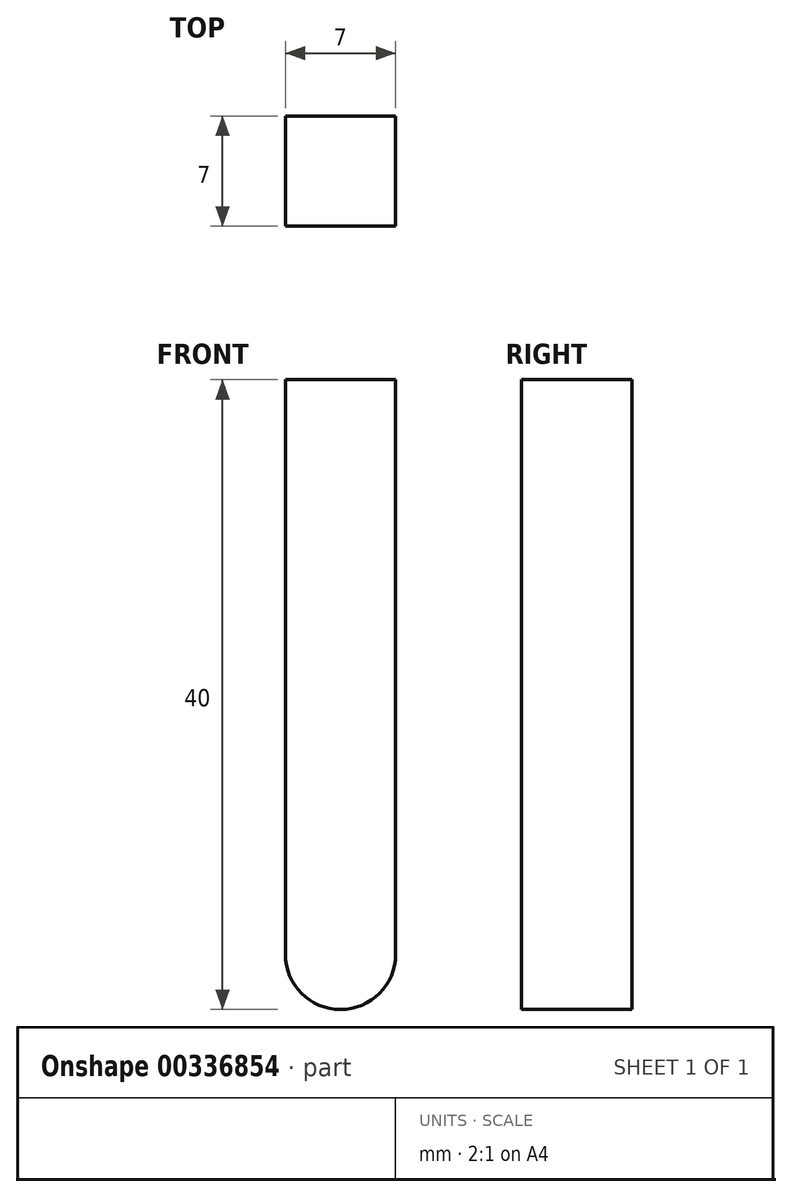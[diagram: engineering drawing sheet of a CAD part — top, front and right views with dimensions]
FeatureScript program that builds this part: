
annotation { "Feature Type Name" : "Feature", "Feature Type Description" : "" }
export const myFeature = defineFeature(function(context is Context, id is Id, definition is map)
    precondition{}
    {
        {
            var Q0;
            Q0=qCreatedBy(makeId("Front.planeOp"),FACE);
            var sketch = newSketch(context, id + "F0", { "sketchPlane" : qUnion([Q0])});
            skLineSegment(sketch, "E0.bottom", {"start": v(3.5, 20) * mm, "end": v(-3.5, 20) * mm});
            skLineSegment(sketch, "E0.top", {"start": v(3.5, -20) * mm, "end": v(-3.5, -20) * mm});
            skLineSegment(sketch, "E0.left", {"start": v(3.5, 20) * mm, "end": v(3.5, -20) * mm});
            skLineSegment(sketch, "E0.right", {"start": v(-3.5, 20) * mm, "end": v(-3.5, -20) * mm});
            skPoint(sketch, "E0.middle", {"position": v(0, 0) * mm});
            skSolve(sketch);
        }
        {
            var Q0;
            Q0=makeQuery(id+"F0.imprint","IMPRINT",FACE,{"disambiguationData":[TD([[makeQuery(id+"F0.imprint","IMPRINT",EDGE,{"derivedFrom":sQuery(id+"F0.wireOp",EDGE,"E0.bottom")}),1.0]])]});
            extrude(context, id + "F1", {"entities" : qUnion([Q0]), "depth" : 7 * mm});
        }
        {
            var Q0;
            Q0=makeQuery(id+"F1.opExtrude","SWEPT_EDGE",EDGE,{"disambiguationData":[OSD([sQuery(id+"F0.wireOp",EDGE,"E0.top"),sQuery(id+"F0.wireOp",EDGE,"E0.left")])]});
            var Q1;
            Q1=makeQuery(id+"F1.opExtrude","SWEPT_EDGE",EDGE,{"disambiguationData":[OSD([sQuery(id+"F0.wireOp",EDGE,"E0.top"),sQuery(id+"F0.wireOp",EDGE,"E0.right")])]});
            fillet(context, id + "F2", {"entities" : qUnion([Q0, Q1]), "radius" : 3.5 * mm, "tangentPropagation" : true, "allowEdgeOverflow" : false});
        }
    });
